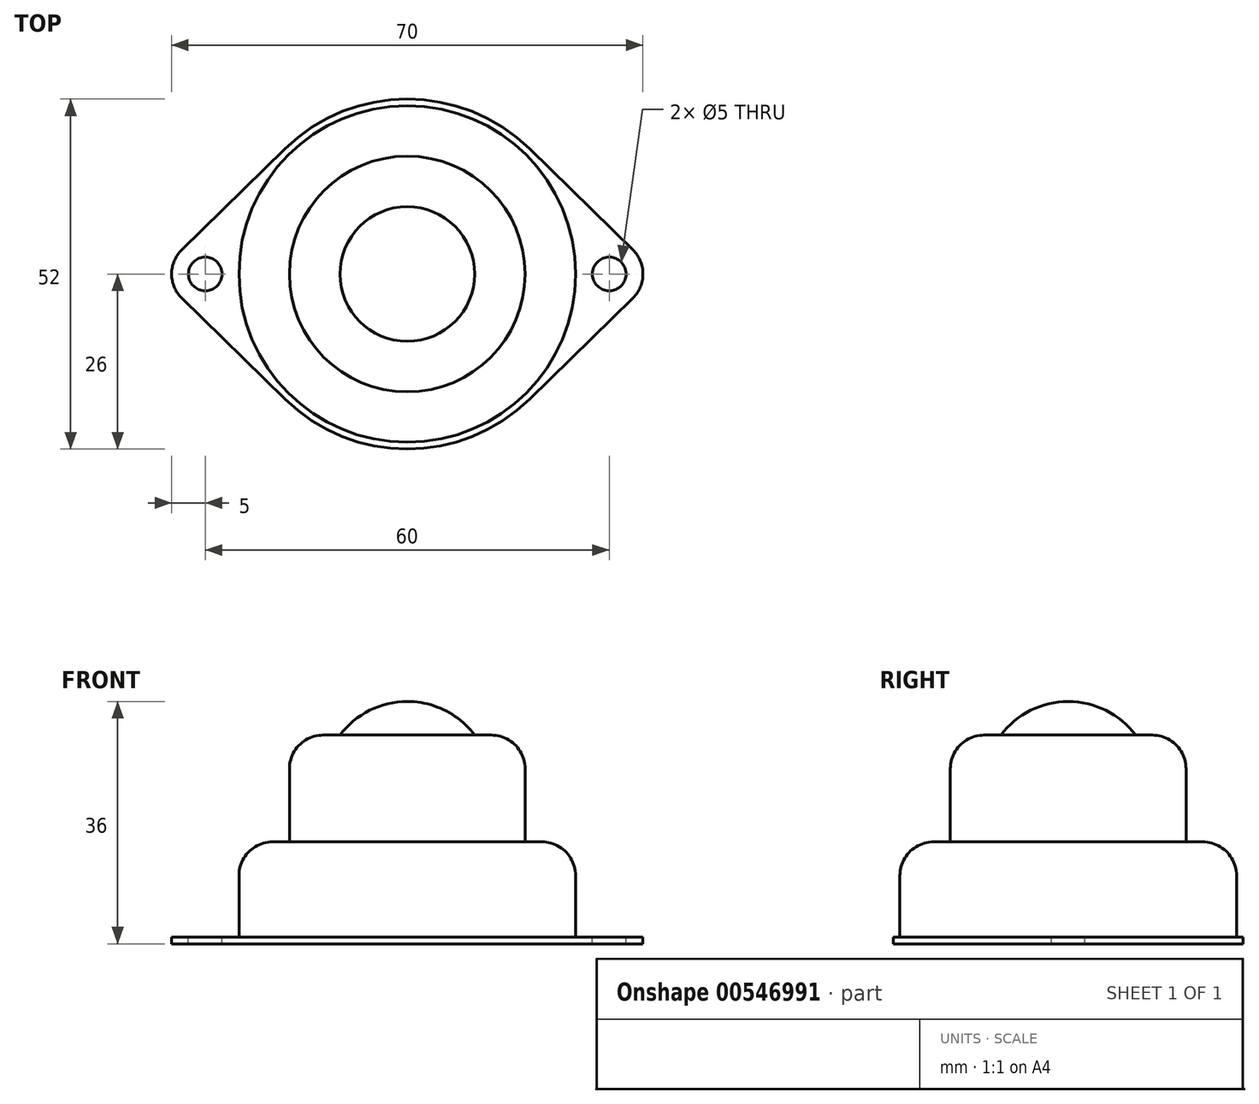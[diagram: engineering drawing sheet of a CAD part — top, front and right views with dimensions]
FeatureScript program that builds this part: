
annotation { "Feature Type Name" : "Feature", "Feature Type Description" : "" }
export const myFeature = defineFeature(function(context is Context, id is Id, definition is map)
    precondition{}
    {
        {
            var Q0;
            Q0=qCreatedBy(makeId("Front.planeOp"),FACE);
            var sketch = newSketch(context, id + "F0", { "sketchPlane" : qUnion([Q0])});
            skLineSegment(sketch, "E0.bottom", {"start": v(-25, 0) * mm, "end": v(0, 0) * mm});
            skLineSegment(sketch, "E0.right", {"start": v(0, 0) * mm, "end": v(0, 35) * mm});
            skLineSegment(sketch, "E1", {"start": v(-25, 14.13) * mm, "end": v(-17.5, 14.13) * mm});
            skLineSegment(sketch, "E2", {"start": v(-17.5, 14.13) * mm, "end": v(-17.5, 30) * mm});
            skLineSegment(sketch, "E3", {"start": v(-17.5, 30) * mm, "end": v(-10, 30) * mm});
            skArc(sketch, "E4", {"start": v(-10, 30) * mm, "mid": v(-5.6, 33.68) * mm, "end": v(0, 35) * mm});
            skLineSegment(sketch, "E5", {"start": v(-25, 14.13) * mm, "end": v(-25, 0) * mm});
            skSolve(sketch);
        }
        {
            var Q0;
            Q0=makeQuery(id+"F0.imprint","IMPRINT",FACE,{"disambiguationData":[TD([[makeQuery(id+"F0.imprint","IMPRINT",EDGE,{"derivedFrom":sQuery(id+"F0.wireOp",EDGE,"E0.bottom")}),1.0]])]});
            var Q1;
            Q1=sQuery(id+"F0.wireOp",EDGE,"E0.right");
            revolve(context, id + "F1", {"entities" : qUnion([Q0]), "axis" : qUnion([Q1]), "revolveType" : RevolveType.FULL});
        }
        {
            var Q0;
            Q0=makeQuery(id+"F1.opRevolve","SWEPT_EDGE",EDGE,{"disambiguationData":[OSD([sQuery(id+"F0.wireOp",EDGE,"E2"),sQuery(id+"F0.wireOp",EDGE,"E3")])]});
            var Q1;
            Q1=makeQuery(id+"F1.opRevolve","SWEPT_EDGE",EDGE,{"disambiguationData":[OSD([sQuery(id+"F0.wireOp",EDGE,"E1"),sQuery(id+"F0.wireOp",EDGE,"E5")])]});
            fillet(context, id + "F2", {"entities" : qUnion([Q0, Q1]), "radius" : 5 * mm, "tangentPropagation" : true, "allowEdgeOverflow" : false});
        }
        {
            var Q0;
            Q0=makeQuery(id+"F1.opRevolve","SWEPT_FACE",FACE,{"disambiguationData":[OSD([sQuery(id+"F0.wireOp",EDGE,"E0.bottom")])]});
            var sketch = newSketch(context, id + "F3", { "sketchPlane" : qUnion([Q0])});
            skLineSegment(sketch, "E6", {"start": v(-35, 0) * mm, "end": v(35, 0) * mm});
            skCircle(sketch, "E7", {"center": v(-30, 0) * mm, "radius": 2.5 * mm});
            skCircle(sketch, "E8", {"center": v(30, 0) * mm, "radius": 2.5 * mm});
            skArc(sketch, "E9", {"start": v(-33.5, 3.57) * mm, "mid": v(-35, 0) * mm, "end": v(-33.5, -3.57) * mm});
            skArc(sketch, "E10", {"start": v(33.5, 3.57) * mm, "mid": v(35, 0) * mm, "end": v(33.5, -3.57) * mm});
            skArc(sketch, "E11", {"start": v(-18.2, 18.57) * mm, "mid": v(0, 26) * mm, "end": v(18.2, 18.57) * mm});
            skArc(sketch, "E12", {"start": v(-18.2, -18.57) * mm, "mid": v(0, -26) * mm, "end": v(18.2, -18.57) * mm});
            skLineSegment(sketch, "E13", {"start": v(-18.2, 18.57) * mm, "end": v(-33.5, 3.57) * mm});
            skLineSegment(sketch, "E14", {"start": v(18.2, 18.57) * mm, "end": v(33.5, 3.57) * mm});
            skLineSegment(sketch, "E15", {"start": v(-33.5, -3.57) * mm, "end": v(-18.2, -18.57) * mm});
            skLineSegment(sketch, "E16", {"start": v(33.5, -3.57) * mm, "end": v(18.2, -18.57) * mm});
            skSolve(sketch);
        }
        {
            var Q0;
            Q0 = qSketchRegion(id + "F3", true);
            extrude(context, id + "F4", {"entities" : qUnion([Q0]), "operationType" : NewBodyOperationType.ADD, "depth" : 1 * mm, "offsetDistance" : 25 * mm});
        }
    });
